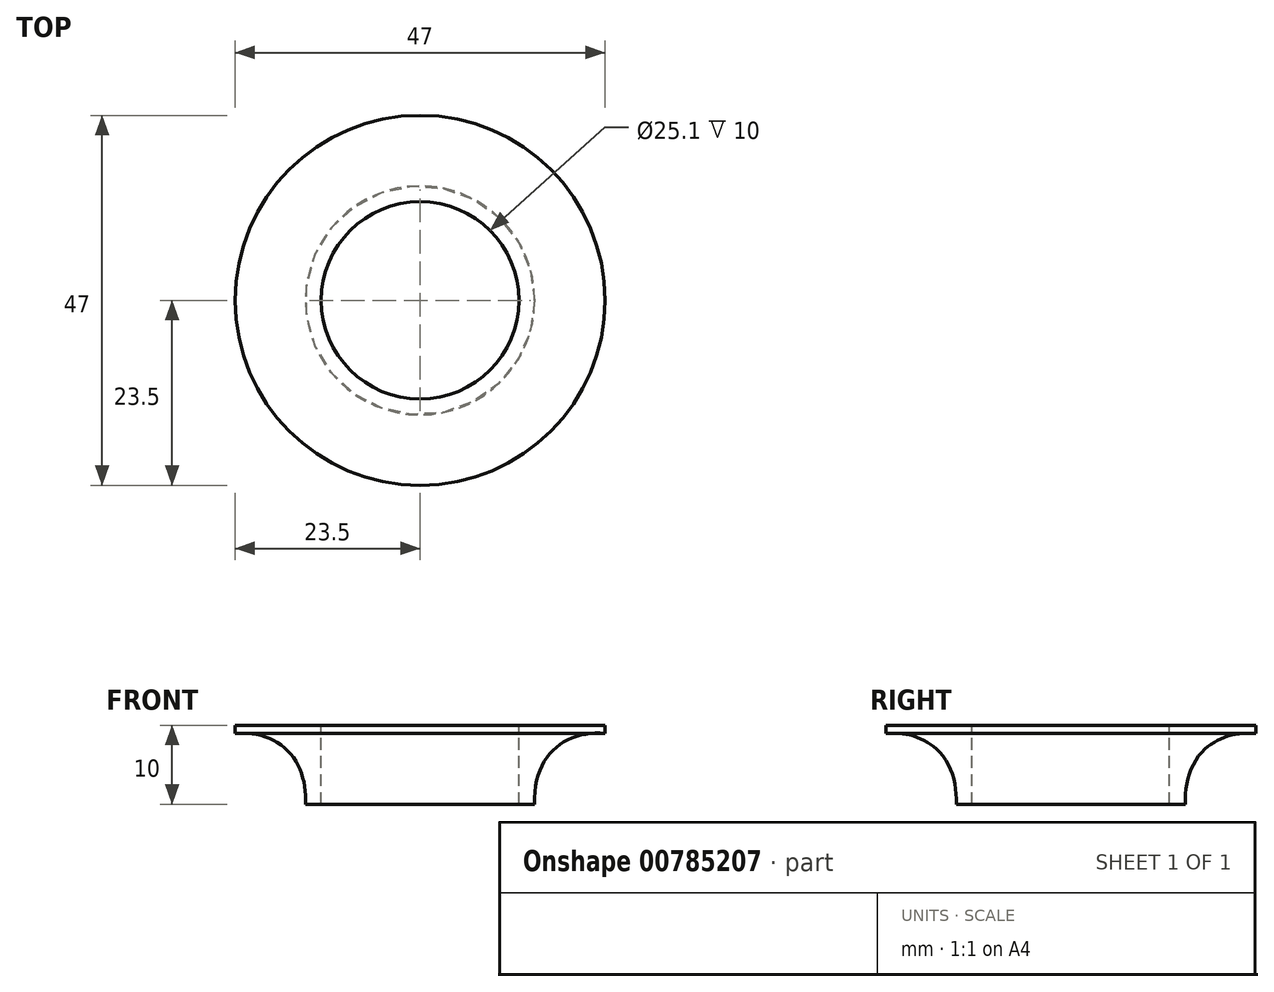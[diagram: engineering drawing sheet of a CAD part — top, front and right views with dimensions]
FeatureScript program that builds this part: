
annotation { "Feature Type Name" : "Feature", "Feature Type Description" : "" }
export const myFeature = defineFeature(function(context is Context, id is Id, definition is map)
    precondition{}
    {
        {
            var Q0;
            Q0=qCreatedBy(makeId("Front.planeOp"),FACE);
            var sketch = newSketch(context, id + "F0", { "sketchPlane" : qUnion([Q0])});
            skLineSegment(sketch, "E0", {"start": v(0, 39.5) * mm, "end": v(0, -36.43) * mm, "construction": true});
            skLineSegment(sketch, "E1", {"start": v(-14.77, 10) * mm, "end": v(-47.9, 10) * mm, "construction": true});
            skCircle(sketch, "E2", {"center": v(0, 10) * mm, "radius": 12.55 * mm, "construction": true});
            skLineSegment(sketch, "E3", {"start": v(12.55, 10) * mm, "end": v(12.55, 0) * mm});
            skLineSegment(sketch, "E4", {"start": v(12.55, 0) * mm, "end": v(14.55, 0) * mm});
            skLineSegment(sketch, "E5", {"start": v(23.5, 10) * mm, "end": v(23.5, 9) * mm});
            skLineSegment(sketch, "E6", {"start": v(12.55, 10) * mm, "end": v(23.5, 10) * mm});
            skFitSpline(sketch, "E7", {"points": [v(23.5, 9) * mm, v(14.55, 0) * mm], "startDerivative": vector(-14.8, 1.14) * mm, "endDerivative": vector(0.72, -19.05) * mm});
            skSolve(sketch);
        }
        {
            var Q0;
            Q0=makeQuery(id+"F0.imprint","IMPRINT",FACE,{"disambiguationData":[TD([[makeQuery(id+"F0.imprint","IMPRINT",EDGE,{"derivedFrom":sQuery(id+"F0.wireOp",EDGE,"E3")}),1.0]])]});
            var Q1;
            Q1=sQuery(id+"F0.wireOp",EDGE,"E0");
            revolve(context, id + "F1", {"surfaceOperationType" : NewSurfaceOperationType.NEW, "entities" : qUnion([Q0]), "axis" : qUnion([Q1]), "revolveType" : RevolveType.FULL});
        }
    });
